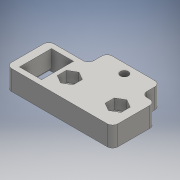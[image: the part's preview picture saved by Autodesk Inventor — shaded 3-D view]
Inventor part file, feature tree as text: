
AUTODESK INVENTOR PART (.ipt)
format: ipt  version: 2016 SP1 (Build 200210100, 210)  size: 195,072 bytes
history: native  units: mm
features: extrude x5, sketch x5, reference x3, fillet x1, projected_geometry x1
ambient origin geometry x8: Origin, YZ Plane, XZ Plane, XY Plane, X Axis, Y Axis, Z Axis, Center Point
bodies: Solid1 (feature_tree)
feature tree (15):
  extrude  "Extrusion1"  Depth=3.0mm
  extrude  "Extrusion2"  Depth=4.0mm
  extrude  "Extrusion3"  Depth=1.0mm
  extrude  "Extrusion4"  Depth=1.0mm
  fillet  "Fillet1"  Radius=7.5mm
  extrude  "Extrusion5"  Depth=6.0mm
  sketch  "Sketch1"  dims[d0=3.0mm d1=3.0mm]
  reference  "Reference1"
  reference  "Reference2"
  sketch  "Sketch2"  dims[d2=3.0mm d3=4.0mm]
  sketch  "Sketch3"  dims[d4=1.0mm d5=1.0mm]
  reference  "Reference3"
  sketch  "Sketch4"  dims[d6=1.0mm d7=1.0mm d8=7.5mm d9=0.0mm]
  projected_geometry  "Projected Loop1"
  sketch  "Sketch5"  dims[d10=6.0mm d11=6.0mm d12=4.0mm d13=0.0mm d14=20.0mm d15=2.8mm d16=1.4mm d17=10.0mm d18=7.0mm d19=0.0mm d20=3.0mm d21=20.0mm d22=7.0mm d23=3.5mm d24=10.0mm d25=7.0mm d26=0.0mm d27=2.0mm d28=12.0mm d29=36.6mm d30=18.3mm d31=6.0mm d32=1.0mm d33=0.0mm]
